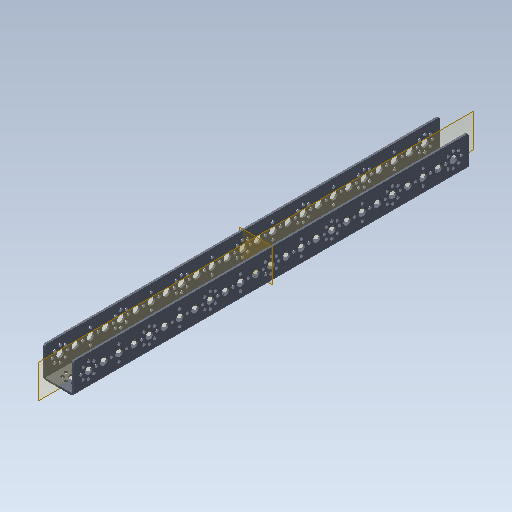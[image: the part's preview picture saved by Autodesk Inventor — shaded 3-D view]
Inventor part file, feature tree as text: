
AUTODESK INVENTOR PART (.ipt)
format: ipt  version: 2020 (Build 240168000, 168)  size: 633,344 bytes
history: native  units: in
note: dims shown in document units (in); Inventor stores cm internally (conversion verified against a paired STEP export)
features: other x216, plane x2, imported_body x1
ambient origin geometry x8: Origin, YZ Plane, XZ Plane, XY Plane, X Axis, Y Axis, Z Axis, Center Point
bodies: Body1 (feature_tree)
feature tree (219):
  other  "tetrix_739069_2012"
  other  "tetrix_739069_20121"
  other  "A_1"
  other  "A_78"
  other  "A_79"
  other  "A_80"
  other  "A_81"
  other  "A_82"
  other  "A_83"
  other  "A_84"
  other  "A_85"
  other  "A_27"
  other  "A_86"
  other  "A_87"
  other  "A_88"
  other  "A_89"
  other  "A_90"
  other  "A_91"
  other  "A_92"
  other  "A_93"
  other  "A_119"
  other  "A_120"
  other  "A_121"
  other  "A_122"
  other  "A_123"
  other  "A_124"
  other  "A_125"
  other  "A_126"
  other  "A_127"
  other  "A_149"
  other  "A_150"
  other  "A_151"
  other  "A_152"
  other  "A_153"
  other  "A_154"
  other  "A_155"
  other  "A_156"
  other  "A_157"
  other  "A_158"
  other  "A_159"
  other  "A_160"
  other  "A_161"
  other  "A_162"
  other  "A_163"
  other  "A_164"
  other  "A_165"
  other  "A_166"
  other  "Work Axis46"
  other  "Work Axis47"
  other  "Work Axis48"
  other  "Work Axis49"
  other  "Work Axis50"
  other  "Work Axis51"
  other  "Work Axis52"
  other  "Work Axis53"
  other  "Work Axis54"
  other  "Work Axis55"
  other  "Work Axis56"
  other  "Work Axis57"
  other  "Work Axis58"
  other  "Work Axis59"
  other  "Work Axis60"
  other  "Work Axis61"
  other  "Work Axis62"
  other  "Work Axis63"
  other  "A_18"
  other  "A_94"
  other  "A_95"
  other  "A_96"
  other  "A_97"
  other  "A_98"
  other  "A_99"
  other  "A_100"
  other  "A_101"
  other  "A_31"
  other  "A_102"
  other  "A_103"
  other  "A_104"
  other  "A_105"
  other  "A_106"
  other  "A_107"
  other  "A_108"
  other  "A_109"
  other  "A_128"
  other  "A_129"
  other  "A_130"
  other  "A_131"
  other  "A_132"
  other  "A_133"
  other  "A_134"
  other  "A_135"
  other  "A_136"
  other  "A_1283"
  other  "A_1284"
  other  "A_1285"
  other  "A_1286"
  other  "A_1287"
  other  "A_1288"
  other  "A_1289"
  other  "A_1290"
  other  "A_1291"
  other  "A_1292"
  other  "A_1293"
  other  "A_1294"
  other  "A_1295"
  other  "A_1296"
  other  "A_1297"
  other  "A_1298"
  other  "A_1299"
  other  "A_1300"
  other  "Work Axis109"
  other  "Work Axis110"
  other  "Work Axis111"
  other  "Work Axis112"
  other  "Work Axis113"
  other  "Work Axis114"
  other  "Work Axis115"
  other  "Work Axis116"
  other  "Work Axis117"
  other  "Work Axis118"
  other  "Work Axis119"
  other  "Work Axis120"
  other  "Work Axis121"
  other  "Work Axis122"
  other  "Work Axis123"
  other  "Work Axis124"
  other  "Work Axis125"
  other  "Work Axis126"
  other  "A_77"
  other  "A_110"
  other  "A_111"
  other  "A_112"
  other  "A_113"
  other  "A_139"
  other  "A_140"
  other  "A_141"
  other  "A_142"
  other  "A_143"
  other  "A_2421"
  other  "A_2422"
  other  "A_2423"
  other  "A_2424"
  other  "A_2425"
  other  "A_2426"
  other  "A_2427"
  other  "A_2428"
  other  "A_2429"
  other  "A_2430"
  other  "A_2449"
  other  "A_2450"
  other  "A_2451"
  other  "A_2452"
  other  "A_2453"
  other  "A_2454"
  other  "A_2455"
  other  "A_2456"
  other  "A_2457"
  other  "A_2458"
  other  "A_114"
  other  "A_115"
  other  "A_116"
  other  "A_117"
  other  "A_118"
  other  "A_144"
  other  "A_145"
  other  "A_146"
  other  "A_147"
  other  "A_148"
  other  "A_2431"
  other  "A_2432"
  other  "A_2433"
  other  "A_2434"
  other  "A_2435"
  other  "A_2436"
  other  "A_2437"
  other  "A_2438"
  other  "A_2439"
  other  "A_2440"
  other  "A_2459"
  other  "A_2460"
  other  "A_2461"
  other  "A_2462"
  other  "A_2463"
  other  "A_2464"
  other  "A_2465"
  other  "A_2466"
  other  "A_2467"
  other  "A_2468"
  other  "A_75"
  other  "A_76"
  other  "A_137"
  other  "A_138"
  other  "A_2441"
  other  "A_2442"
  other  "A_2443"
  other  "A_2444"
  other  "A_2469"
  other  "A_2470"
  other  "A_2471"
  other  "A_2472"
  other  "A_2417"
  other  "A_2418"
  other  "A_2419"
  other  "A_2420"
  other  "A_2445"
  other  "A_2446"
  other  "A_2447"
  other  "A_2448"
  other  "A_2473"
  other  "A_2474"
  other  "A_2475"
  other  "A_2476"
  other  "FRONT"
  other  "TOP"
  other  "RIGHT"
  other  "DTM1"
  plane  "Work Plane5"
  plane  "Work Plane6"
  imported_body  "Base1"
